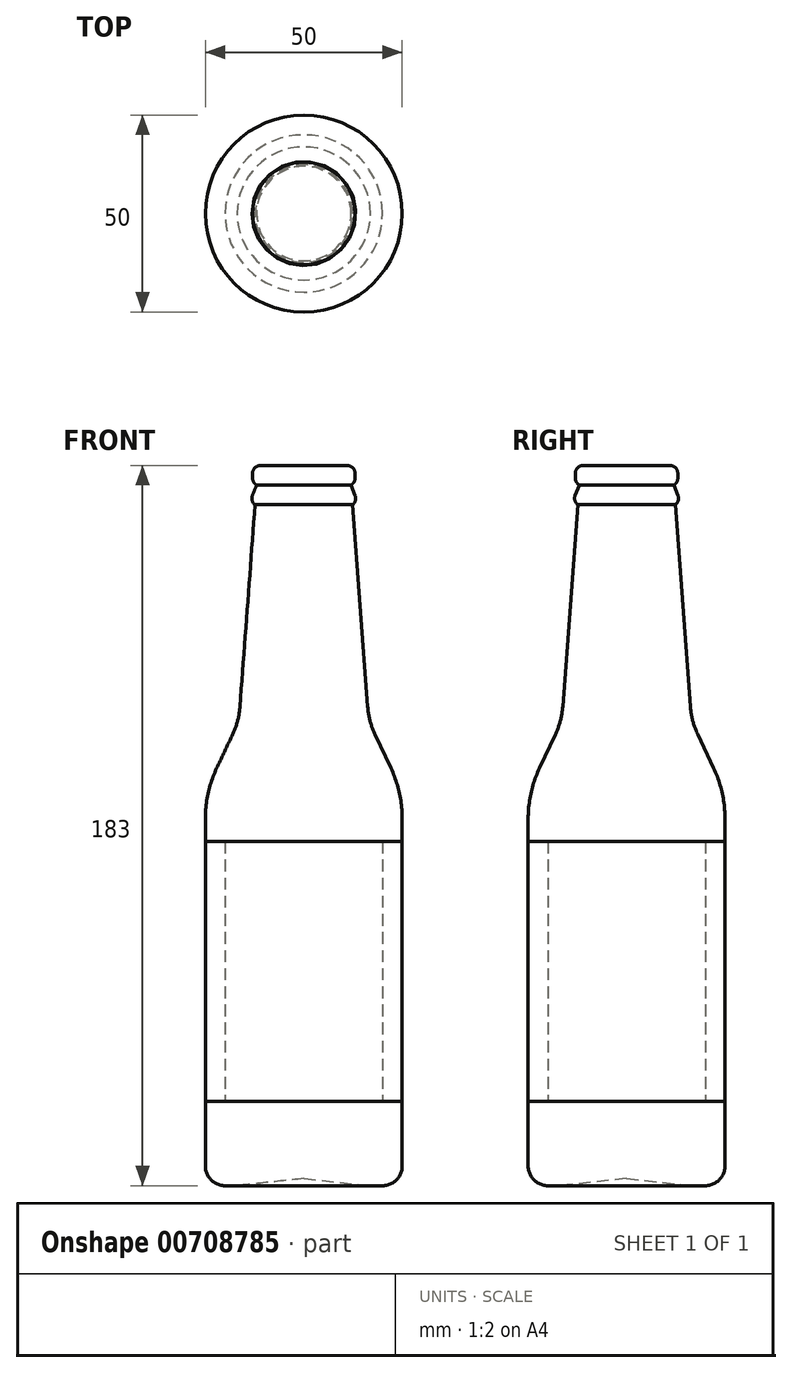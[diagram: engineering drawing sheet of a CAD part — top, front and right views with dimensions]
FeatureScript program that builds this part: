
annotation { "Feature Type Name" : "Feature", "Feature Type Description" : "" }
export const myFeature = defineFeature(function(context is Context, id is Id, definition is map)
    precondition{}
    {
        {
            var Q0;
            Q0=qCreatedBy(makeId("Front.planeOp"),FACE);
            var sketch = newSketch(context, id + "F0", { "sketchPlane" : qUnion([Q0])});
            skLineSegment(sketch, "E0.bottom", {"start": v(0, 0) * mm, "end": v(20, 0) * mm});
            skLineSegment(sketch, "E0.top", {"start": v(0, 118) * mm, "end": v(20, 118) * mm});
            skLineSegment(sketch, "E0.left", {"start": v(0, 0) * mm, "end": v(0, 118) * mm});
            skLineSegment(sketch, "E0.right", {"start": v(20, 0) * mm, "end": v(20, 118) * mm});
            skLineSegment(sketch, "E1.bottom", {"start": v(0, 118) * mm, "end": v(0, 118) * mm});
            skLineSegment(sketch, "E2.bottom", {"start": v(0, 118) * mm, "end": v(12, 118) * mm});
            skLineSegment(sketch, "E2.top", {"start": v(0, 178) * mm, "end": v(12, 178) * mm});
            skLineSegment(sketch, "E2.left", {"start": v(0, 118) * mm, "end": v(0, 178) * mm});
            skLineSegment(sketch, "E2.right", {"start": v(12, 118) * mm, "end": v(12, 178) * mm});
            skLineSegment(sketch, "E3.top", {"start": v(0, 183) * mm, "end": v(13, 183) * mm});
            skLineSegment(sketch, "E3.left", {"start": v(0, 178) * mm, "end": v(0, 183) * mm});
            skLineSegment(sketch, "E3.right", {"start": v(13, 178) * mm, "end": v(13, 183) * mm});
            skLineSegment(sketch, "E4.bottom", {"start": v(20, 0) * mm, "end": v(25, 0) * mm});
            skLineSegment(sketch, "E4.top", {"start": v(20, 100) * mm, "end": v(25, 100) * mm});
            skLineSegment(sketch, "E4.left", {"start": v(20, 0) * mm, "end": v(20, 100) * mm});
            skLineSegment(sketch, "E4.right", {"start": v(25, 0) * mm, "end": v(25, 100) * mm});
            skLineSegment(sketch, "E5", {"start": v(0, 118) * mm, "end": v(16.5, 118) * mm});
            skLineSegment(sketch, "E6", {"start": v(16.5, 118) * mm, "end": v(12, 178) * mm});
            skLineSegment(sketch, "E7", {"start": v(25, 100) * mm, "end": v(16.5, 118) * mm});
            skLineSegment(sketch, "E8.bottom", {"start": v(0, 178) * mm, "end": v(13, 178) * mm});
            skLineSegment(sketch, "E8.top", {"start": v(0, 173) * mm, "end": v(14, 173) * mm});
            skLineSegment(sketch, "E8.left", {"start": v(0, 178) * mm, "end": v(0, 173) * mm});
            skLineSegment(sketch, "E9", {"start": v(14, 173) * mm, "end": v(12, 178) * mm});
            skLineSegment(sketch, "E10.bottom", {"start": v(25, 87.43) * mm, "end": v(20, 87.43) * mm});
            skLineSegment(sketch, "E10.top", {"start": v(25, 21.43) * mm, "end": v(20, 21.43) * mm});
            skLineSegment(sketch, "E10.left", {"start": v(25, 87.43) * mm, "end": v(25, 21.43) * mm});
            skLineSegment(sketch, "E10.right", {"start": v(20, 87.43) * mm, "end": v(20, 21.43) * mm});
            skSolve(sketch);
        }
        {
            var Q0;
            {var subQ0=sQuery(id+"F0.wireOp",EDGE,"E4.bottom");Q0=makeQuery(id+"F0.imprint","IMPRINT",FACE,{"disambiguationData":[TD([[makeQuery(id+"F0.imprint","IMPRINT",EDGE,{"derivedFrom":subQ0}),1.0]])]});}
            var Q1;
            {var subQ7=sQuery(id+"F0.wireOp",EDGE,"E0.bottom");Q1=makeQuery(id+"F0.imprint","IMPRINT",FACE,{"disambiguationData":[TD([[makeQuery(id+"F0.imprint","IMPRINT",EDGE,{"derivedFrom":subQ7}),1.0]])]});}
            var Q2;
            {var subQ0=sQuery(id+"F0.wireOp",EDGE,"E4.top");Q2=makeQuery(id+"F0.imprint","IMPRINT",FACE,{"disambiguationData":[TD([[makeQuery(id+"F0.imprint","IMPRINT",EDGE,{"derivedFrom":subQ0}),1.0]])]});}
            var Q3;
            {var subQ0=sQuery(id+"F0.wireOp",EDGE,"E2.right");var subQ1=sQuery(id+"F0.wireOp",EDGE,"E0.top");var subQ2=makeQuery(id+"F0.imprint","INTERSECT",VERTEX,{"derivedFrom":[subQ1,subQ0]});Q3=makeQuery(id+"F0.imprint","IMPRINT",FACE,{"disambiguationData":[TD([[makeQuery(id+"F0.imprint","IMPRINT",EDGE,{"disambiguationData":[TD([[subQ2,-1.0]])],"derivedFrom":subQ0}),-1.0]])]});}
            var Q4;
            {var subQ1=sQuery(id+"F0.wireOp",EDGE,"E0.top");var subQ3=sQuery(id+"F0.wireOp",EDGE,"E2.right");var subQ4=makeQuery(id+"F0.imprint","INTERSECT",VERTEX,{"derivedFrom":[subQ1,subQ3]});Q4=makeQuery(id+"F0.imprint","IMPRINT",FACE,{"disambiguationData":[TD([[makeQuery(id+"F0.imprint","IMPRINT",EDGE,{"disambiguationData":[TD([[subQ4,-1.0]])],"derivedFrom":subQ3}),1.0]])]});}
            var Q5;
            {var subQ0=sQuery(id+"F0.wireOp",EDGE,"E2.top");Q5=makeQuery(id+"F0.imprint","IMPRINT",FACE,{"disambiguationData":[TD([[makeQuery(id+"F0.imprint","IMPRINT",EDGE,{"derivedFrom":subQ0}),-1.0]])]});}
            var Q6;
            {var subQ0=sQuery(id+"F0.wireOp",EDGE,"E6");var subQ3=sQuery(id+"F0.wireOp",EDGE,"E8.top");var subQ5=makeQuery(id+"F0.imprint","INTERSECT",VERTEX,{"derivedFrom":[subQ0,subQ3]});Q6=makeQuery(id+"F0.imprint","IMPRINT",FACE,{"disambiguationData":[TD([[makeQuery(id+"F0.imprint","IMPRINT",EDGE,{"disambiguationData":[TD([[subQ5,1.0]])],"derivedFrom":subQ3}),1.0]])]});}
            var Q7;
            {var subQ0=sQuery(id+"F0.wireOp",EDGE,"E9");Q7=makeQuery(id+"F0.imprint","IMPRINT",FACE,{"disambiguationData":[TD([[makeQuery(id+"F0.imprint","IMPRINT",EDGE,{"derivedFrom":subQ0}),1.0]])]});}
            var Q8;
            Q8=makeQuery(id+"F0.imprint","IMPRINT",FACE,{"disambiguationData":[TD([[makeQuery(id+"F0.imprint","IMPRINT",EDGE,{"derivedFrom":sQuery(id+"F0.wireOp",EDGE,"E2.top")}),1.0]])]});
            var Q9;
            {var subQ0=sQuery(id+"F0.wireOp",EDGE,"E4.top");Q9=makeQuery(id+"F0.imprint","IMPRINT",FACE,{"disambiguationData":[TD([[makeQuery(id+"F0.imprint","IMPRINT",EDGE,{"derivedFrom":subQ0}),-1.0]])]});}
            var Q10;
            Q10=sQuery(id+"F0.wireOp",EDGE,"E2.left");
            revolve(context, id + "F1", {"surfaceOperationType" : NewSurfaceOperationType.NEW, "entities" : qUnion([Q0, Q1, Q2, Q3, Q4, Q5, Q6, Q7, Q8, Q9]), "axis" : qUnion([Q10]), "revolveType" : RevolveType.FULL});
        }
        {
            var Q0;
            Q0=makeQuery(id+"F1.opRevolve","SWEPT_EDGE",EDGE,{"disambiguationData":[OSD([sQuery(id+"F0.wireOp",EDGE,"E3.top"),sQuery(id+"F0.wireOp",EDGE,"E3.right")])]});
            var Q1;
            Q1=makeQuery(id+"F1.opRevolve","SWEPT_EDGE",EDGE,{"disambiguationData":[OSD([sQuery(id+"F0.wireOp",EDGE,"E8.top"),sQuery(id+"F0.wireOp",EDGE,"E9")])]});
            var Q2;
            Q2=makeQuery(id+"F1.opRevolve","SWEPT_EDGE",EDGE,{"disambiguationData":[OSD([sQuery(id+"F0.wireOp",EDGE,"E3.right"),sQuery(id+"F0.wireOp",EDGE,"E8.bottom")])]});
            fillet(context, id + "F2", {"entities" : qUnion([Q0, Q1, Q2]), "radius" : 2 * mm, "tangentPropagation" : true, "allowEdgeOverflow" : false});
        }
        {
            var Q0;
            Q0=makeQuery(id+"F1.opRevolve","SWEPT_EDGE",EDGE,{"disambiguationData":[OSD([sQuery(id+"F0.wireOp",EDGE,"E4.top"),sQuery(id+"F0.wireOp",EDGE,"E4.right"),sQuery(id+"F0.wireOp",EDGE,"E7")])]});
            fillet(context, id + "F3", {"entities" : qUnion([Q0]), "radius" : 30 * mm, "tangentPropagation" : true, "allowEdgeOverflow" : false});
        }
        {
            var Q0;
            Q0=makeQuery(id+"F1.opRevolve","SWEPT_EDGE",EDGE,{"disambiguationData":[OSD([sQuery(id+"F0.wireOp",EDGE,"E0.top"),sQuery(id+"F0.wireOp",EDGE,"E6"),sQuery(id+"F0.wireOp",EDGE,"E7")])]});
            fillet(context, id + "F4", {"entities" : qUnion([Q0]), "radius" : 20 * mm, "tangentPropagation" : true, "allowEdgeOverflow" : false});
        }
        {
            var Q0;
            Q0=makeQuery(id+"F1.opRevolve","SWEPT_EDGE",EDGE,{"disambiguationData":[OSD([sQuery(id+"F0.wireOp",EDGE,"E4.bottom"),sQuery(id+"F0.wireOp",EDGE,"E4.right")])]});
            fillet(context, id + "F5", {"entities" : qUnion([Q0]), "radius" : 5 * mm, "tangentPropagation" : true, "allowEdgeOverflow" : false});
        }
        {
            var Q0;
            Q0=qCreatedBy(makeId("Front.planeOp"),FACE);
            var sketch = newSketch(context, id + "F6", { "sketchPlane" : qUnion([Q0])});
            skLineSegment(sketch, "E11", {"start": v(0, 0) * mm, "end": v(16.92, 0) * mm});
            skLineSegment(sketch, "E12", {"start": v(16.92, 0) * mm, "end": v(0, 1.8) * mm});
            skLineSegment(sketch, "E13", {"start": v(0, 1.8) * mm, "end": v(0, 0) * mm});
            skSolve(sketch);
        }
        {
            var Q0;
            Q0 = qSketchRegion(id + "F6", true);
            var Q1;
            Q1=sQuery(id+"F6.wireOp",EDGE,"E13");
            revolve(context, id + "F7", {"operationType" : NewBodyOperationType.REMOVE, "surfaceOperationType" : NewSurfaceOperationType.NEW, "entities" : qUnion([Q0]), "axis" : qUnion([Q1]), "revolveType" : RevolveType.FULL, "oppositeDirection" : true});
        }
        {
            var Q0;
            {var subQ2=sQuery(id+"F0.wireOp",EDGE,"E10.bottom");Q0=makeQuery(id+"F0.imprint","IMPRINT",FACE,{"disambiguationData":[TD([[makeQuery(id+"F0.imprint","IMPRINT",EDGE,{"derivedFrom":subQ2}),1.0]])]});}
            var Q1;
            Q1=sQuery(id+"F0.wireOp",EDGE,"E0.left");
            revolve(context, id + "F8", {"surfaceOperationType" : NewSurfaceOperationType.NEW, "entities" : qUnion([Q0]), "axis" : qUnion([Q1]), "revolveType" : RevolveType.FULL});
        }
    });
